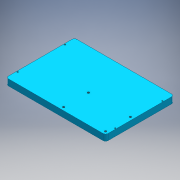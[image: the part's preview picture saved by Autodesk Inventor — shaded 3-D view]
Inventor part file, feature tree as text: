
AUTODESK INVENTOR PART (.ipt)
format: ipt  version: 2016 (Build 200138000, 138)  size: 137,728 bytes
history: native  units: mm
features: sketch x3, hole x2, extrude x1
ambient origin geometry x8: Origin, YZ Plane, XZ Plane, XY Plane, X Axis, Y Axis, Z Axis, Center Point
bodies: Solid1 (feature_tree)
feature tree (6):
  extrude  "Extrusion1"  Depth=110.0mm
  hole  "Hole1"  [1 undecoded]
  hole  "Hole2"  [1 undecoded]
  sketch  "Sketch1"  dims[d0=160.0mm d1=110.0mm]
  sketch  "Sketch2"  dims[d2=55.0mm d3=80.0mm]
  sketch  "Sketch3"  dims[d4=4.0mm d5=10.0mm d6=0.0mm d7=156.6mm d8=76.0mm d9=38.0mm d10=78.3mm d11=2.013mm d12=5.0mm d13=11.0mm d14=2.6mm d15=14.3117mm d16=7.6mm d17=20.594885mm d18=40.0mm d19=67.5mm d20=5.0mm d21=5.0mm d22=3.242mm d23=8.0mm d24=11.0mm d25=2.6mm d26=14.3117mm d27=11.8mm d28=20.594885mm]
note: 2 required parameter values undecoded (feature->parameter linkage not recoverable at this tier; creation-order binding heuristic only, values carry confidence <= 0.55)
